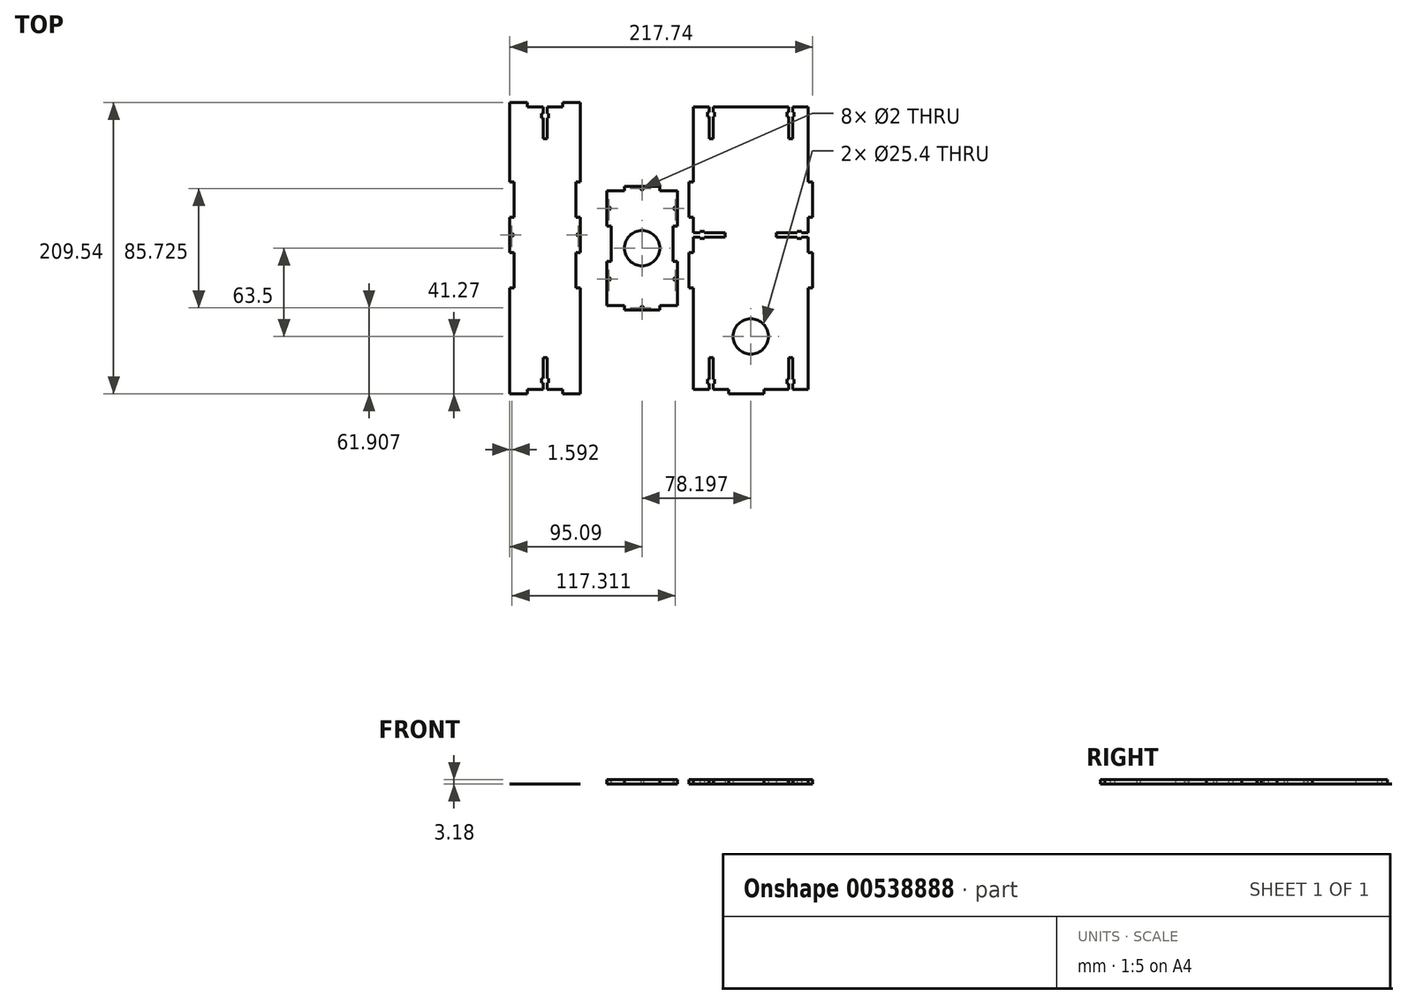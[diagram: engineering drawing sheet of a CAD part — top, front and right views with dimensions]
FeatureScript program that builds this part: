
annotation { "Feature Type Name" : "Feature", "Feature Type Description" : "" }
export const myFeature = defineFeature(function(context is Context, id is Id, definition is map)
    precondition{}
    {
        {
            var Q0;
            Q0=qCreatedBy(makeId("Top.planeOp"),FACE);
            var sketch = newSketch(context, id + "F0", { "sketchPlane" : qUnion([Q0])});
            skLineSegment(sketch, "E0.bottom", {"start": v(-22.22, 41.28) * mm, "end": v(-12.7, 41.28) * mm});
            skLineSegment(sketch, "E0.top", {"start": v(-22.23, -41.28) * mm, "end": v(-12.7, -41.28) * mm});
            skLineSegment(sketch, "E0.left", {"start": v(-22.22, 15.88) * mm, "end": v(-22.23, -9.52) * mm});
            skLineSegment(sketch, "E0.right", {"start": v(22.23, 15.88) * mm, "end": v(22.22, -9.52) * mm});
            skPoint(sketch, "E0.middle", {"position": v(0, 0) * mm});
            skLineSegment(sketch, "E1.bottom", {"start": v(-12.7, 44.45) * mm, "end": v(12.7, 44.45) * mm});
            skLineSegment(sketch, "E1.left", {"start": v(-12.7, 44.45) * mm, "end": v(-12.7, 41.28) * mm});
            skLineSegment(sketch, "E1.right", {"start": v(12.7, 44.45) * mm, "end": v(12.7, 41.28) * mm});
            skPoint(sketch, "E1.middle", {"position": v(0, 41.28) * mm});
            skPoint(sketch, "E2.orphan", {"position": v(12.7, 38.1) * mm});
            skPoint(sketch, "E3.orphan", {"position": v(-12.7, 38.1) * mm});
            skLineSegment(sketch, "E4.top", {"start": v(-12.7, -44.45) * mm, "end": v(12.7, -44.45) * mm});
            skLineSegment(sketch, "E4.left", {"start": v(-12.7, -41.28) * mm, "end": v(-12.7, -44.45) * mm});
            skLineSegment(sketch, "E4.right", {"start": v(12.7, -41.28) * mm, "end": v(12.7, -44.45) * mm});
            skPoint(sketch, "E4.middle", {"position": v(0, -41.27) * mm});
            skPoint(sketch, "E4.bottom.start.orphan", {"position": v(-12.7, -38.1) * mm});
            skPoint(sketch, "E5.orphan", {"position": v(12.7, -38.1) * mm});
            skLineSegment(sketch, "E6.bottom", {"start": v(-22.22, 41.28) * mm, "end": v(-25.4, 41.28) * mm});
            skLineSegment(sketch, "E6.top", {"start": v(-22.22, 15.88) * mm, "end": v(-25.4, 15.88) * mm});
            skLineSegment(sketch, "E6.right", {"start": v(-25.4, 41.28) * mm, "end": v(-25.4, 15.88) * mm});
            skPoint(sketch, "E7", {"position": v(-22.23, -9.52) * mm});
            skLineSegment(sketch, "E8.bottom", {"start": v(-22.23, -9.52) * mm, "end": v(-25.4, -9.52) * mm});
            skLineSegment(sketch, "E8.right", {"start": v(-25.4, -9.52) * mm, "end": v(-25.4, -34.92) * mm});
            skLineSegment(sketch, "E9.MirrorCS", {"start": v(25.4, 41.27) * mm, "end": v(25.4, 15.87) * mm});
            skLineSegment(sketch, "E10.MirrorCS", {"start": v(22.23, 41.28) * mm, "end": v(25.4, 41.28) * mm});
            skLineSegment(sketch, "E11.MirrorCS", {"start": v(22.23, 15.88) * mm, "end": v(25.4, 15.88) * mm});
            skLineSegment(sketch, "E12.MirrorCS", {"start": v(22.23, -9.52) * mm, "end": v(25.4, -9.52) * mm});
            skLineSegment(sketch, "E13.MirrorCS", {"start": v(25.4, -9.53) * mm, "end": v(25.4, -34.93) * mm});
            skLineSegment(sketch, "E14.trimOffspring", {"start": v(12.7, 41.28) * mm, "end": v(22.23, 41.28) * mm});
            skLineSegment(sketch, "E15.trimOffspring", {"start": v(12.7, -41.28) * mm, "end": v(22.23, -41.28) * mm});
            skLineSegment(sketch, "E16.top", {"start": v(-22.22, -41.28) * mm, "end": v(-25.4, -41.28) * mm});
            skLineSegment(sketch, "E16.right", {"start": v(-25.4, -34.92) * mm, "end": v(-25.4, -41.28) * mm});
            skLineSegment(sketch, "E17.bottom", {"start": v(22.22, -41.28) * mm, "end": v(25.4, -41.28) * mm});
            skLineSegment(sketch, "E17.right", {"start": v(25.4, -41.28) * mm, "end": v(25.4, -34.93) * mm});
            skCircle(sketch, "E18", {"center": v(0, 42.86) * mm, "radius": 1 * mm});
            skPoint(sketch, "E18.centerSnap0", {"position": v(-12.7, 42.86) * mm});
            skCircle(sketch, "E19", {"center": v(-23.81, 28.58) * mm, "radius": 1 * mm});
            skPoint(sketch, "E19.centerSnap0", {"position": v(-23.81, 41.28) * mm});
            skPoint(sketch, "E19.centerSnap1", {"position": v(-25.4, 28.58) * mm});
            skCircle(sketch, "E20", {"center": v(23.81, 28.57) * mm, "radius": 1 * mm});
            skPoint(sketch, "E20.centerSnap0", {"position": v(25.4, 28.57) * mm});
            skPoint(sketch, "E20.centerSnap1", {"position": v(23.81, 41.28) * mm});
            skCircle(sketch, "E21", {"center": v(0, -42.86) * mm, "radius": 1 * mm});
            skPoint(sketch, "E21.centerSnap0", {"position": v(0, -44.45) * mm});
            skPoint(sketch, "E21.centerSnap1", {"position": v(-12.7, -42.86) * mm});
            skCircle(sketch, "E22", {"center": v(-23.81, -22.22) * mm, "radius": 1 * mm});
            skPoint(sketch, "E22.centerSnap0", {"position": v(-23.81, -9.52) * mm});
            skPoint(sketch, "E22.centerSnap1", {"position": v(-25.4, -22.22) * mm});
            skCircle(sketch, "E23", {"center": v(23.81, -22.23) * mm, "radius": 1 * mm});
            skPoint(sketch, "E23.centerSnap0", {"position": v(23.81, -9.52) * mm});
            skPoint(sketch, "E23.centerSnap1", {"position": v(25.4, -22.23) * mm});
            skLineSegment(sketch, "E24.direction1", {"start": v(-25.4, -41.28) * mm, "end": v(228.6, -41.28) * mm, "construction": true});
            skCircle(sketch, "E25", {"center": v(0, 0) * mm, "radius": 12.7 * mm});
            skSolve(sketch);
        }
        {
            var Q0;
            Q0=qCreatedBy(makeId("Top.planeOp"),FACE);
            var sketch = newSketch(context, id + "F1", { "sketchPlane" : qUnion([Q0])});
            skLineSegment(sketch, "E26.bottom", {"start": v(-82.39, 101.6) * mm, "end": v(-56.99, 101.6) * mm});
            skLineSegment(sketch, "E26.top", {"start": v(-82.39, -101.6) * mm, "end": v(-56.99, -101.6) * mm});
            skLineSegment(sketch, "E26.left", {"start": v(-95.09, 101.6) * mm, "end": v(-95.09, 47.62) * mm});
            skLineSegment(sketch, "E26.right", {"start": v(-44.29, 101.6) * mm, "end": v(-44.29, 47.63) * mm});
            skPoint(sketch, "E26.middle", {"position": v(-69.69, 0) * mm});
            skLineSegment(sketch, "E27.bottom", {"start": v(-95.09, 104.78) * mm, "end": v(-82.39, 104.78) * mm});
            skLineSegment(sketch, "E27.left", {"start": v(-95.09, 104.78) * mm, "end": v(-95.09, 101.6) * mm});
            skLineSegment(sketch, "E27.right", {"start": v(-44.29, 104.78) * mm, "end": v(-44.29, 101.6) * mm});
            skPoint(sketch, "E27.middle", {"position": v(-69.69, 101.6) * mm});
            skPoint(sketch, "E27.top.start.orphan", {"position": v(-95.09, 98.43) * mm});
            skPoint(sketch, "E28.orphan", {"position": v(-44.29, 98.43) * mm});
            skPoint(sketch, "E29", {"position": v(-82.39, 104.78) * mm});
            skPoint(sketch, "E30", {"position": v(-56.99, 104.78) * mm});
            skLineSegment(sketch, "E31", {"start": v(-82.39, 104.78) * mm, "end": v(-82.39, 101.6) * mm});
            skLineSegment(sketch, "E32", {"start": v(-56.99, 104.78) * mm, "end": v(-56.99, 101.6) * mm});
            skLineSegment(sketch, "E33.trimOffspring", {"start": v(-56.99, 104.78) * mm, "end": v(-44.29, 104.78) * mm});
            skLineSegment(sketch, "E34.MirrorCS", {"start": v(-95.09, -104.78) * mm, "end": v(-82.39, -104.78) * mm});
            skLineSegment(sketch, "E35.MirrorCS", {"start": v(-95.09, -104.78) * mm, "end": v(-95.09, -101.6) * mm});
            skLineSegment(sketch, "E36.MirrorCS", {"start": v(-82.39, -104.78) * mm, "end": v(-82.39, -101.6) * mm});
            skLineSegment(sketch, "E37.MirrorCS", {"start": v(-56.99, -104.78) * mm, "end": v(-56.99, -101.6) * mm});
            skLineSegment(sketch, "E38.MirrorCS", {"start": v(-56.99, -104.78) * mm, "end": v(-44.29, -104.78) * mm});
            skLineSegment(sketch, "E39", {"start": v(-44.29, -104.78) * mm, "end": v(-44.29, -101.6) * mm});
            skPoint(sketch, "E40", {"position": v(-95.09, 47.63) * mm});
            skPoint(sketch, "E41", {"position": v(-95.09, -50.8) * mm});
            skLineSegment(sketch, "E42.bottom", {"start": v(-95.09, 47.63) * mm, "end": v(-91.91, 47.63) * mm});
            skLineSegment(sketch, "E42.top", {"start": v(-95.09, 22.23) * mm, "end": v(-91.91, 22.23) * mm});
            skLineSegment(sketch, "E42.right", {"start": v(-91.91, 47.63) * mm, "end": v(-91.91, 22.23) * mm});
            skLineSegment(sketch, "E43.bottom", {"start": v(-95.09, -3.17) * mm, "end": v(-91.91, -3.17) * mm});
            skLineSegment(sketch, "E43.top", {"start": v(-95.09, -28.58) * mm, "end": v(-91.91, -28.58) * mm});
            skLineSegment(sketch, "E43.right", {"start": v(-91.91, -3.17) * mm, "end": v(-91.91, -28.58) * mm});
            skLineSegment(sketch, "E44.trimOffspring", {"start": v(-95.09, -28.57) * mm, "end": v(-95.09, -101.6) * mm});
            skLineSegment(sketch, "E45.trimOffspring", {"start": v(-95.09, 22.23) * mm, "end": v(-95.09, -3.17) * mm});
            skLineSegment(sketch, "E46.MirrorCS", {"start": v(-47.46, 47.63) * mm, "end": v(-47.46, 22.23) * mm});
            skLineSegment(sketch, "E47.MirrorCS", {"start": v(-47.46, -3.17) * mm, "end": v(-47.46, -28.57) * mm});
            skLineSegment(sketch, "E48.MirrorCS", {"start": v(-44.29, 47.63) * mm, "end": v(-47.46, 47.63) * mm});
            skLineSegment(sketch, "E49.MirrorCS", {"start": v(-44.29, 22.23) * mm, "end": v(-47.46, 22.23) * mm});
            skLineSegment(sketch, "E50.trimOffspring", {"start": v(-44.29, 22.23) * mm, "end": v(-44.29, -3.17) * mm});
            skPoint(sketch, "E51", {"position": v(-44.29, -3.17) * mm});
            skPoint(sketch, "E52", {"position": v(-44.29, -28.57) * mm});
            skLineSegment(sketch, "E53.trimOffspring", {"start": v(-44.29, -28.57) * mm, "end": v(-44.29, -101.6) * mm});
            skLineSegment(sketch, "E54", {"start": v(-44.29, -3.17) * mm, "end": v(-47.46, -3.17) * mm});
            skLineSegment(sketch, "E55", {"start": v(-47.46, -28.57) * mm, "end": v(-44.29, -28.57) * mm});
            skPoint(sketch, "E56.orphan", {"position": v(-44.29, 0) * mm});
            skPoint(sketch, "E57.start.orphan", {"position": v(-95.09, 0) * mm});
            skLineSegment(sketch, "E58.bottom", {"start": v(-71.19, 78.7) * mm, "end": v(-68.19, 78.74) * mm});
            skLineSegment(sketch, "E58.left", {"start": v(-71.19, 78.7) * mm, "end": v(-71.19, 93.66) * mm});
            skLineSegment(sketch, "E58.right", {"start": v(-68.19, 78.74) * mm, "end": v(-68.19, 93.66) * mm});
            skPoint(sketch, "E58.top.end.orphan", {"position": v(-68.19, 124.5) * mm});
            skPoint(sketch, "E59.orphan", {"position": v(-71.19, 124.46) * mm});
            skLineSegment(sketch, "E60.bottom", {"start": v(-72.23, 96.84) * mm, "end": v(-71.19, 96.84) * mm});
            skLineSegment(sketch, "E60.top", {"start": v(-72.23, 93.66) * mm, "end": v(-71.19, 93.66) * mm});
            skLineSegment(sketch, "E60.left", {"start": v(-72.23, 96.84) * mm, "end": v(-72.23, 93.66) * mm});
            skLineSegment(sketch, "E60.right", {"start": v(-67.15, 96.84) * mm, "end": v(-67.15, 93.66) * mm});
            skPoint(sketch, "E60.middle", {"position": v(-69.69, 95.25) * mm});
            skLineSegment(sketch, "E61.trimOffspring", {"start": v(-68.19, 96.84) * mm, "end": v(-67.15, 96.84) * mm});
            skLineSegment(sketch, "E62.trimOffspring", {"start": v(-68.19, 93.66) * mm, "end": v(-67.15, 93.66) * mm});
            skLineSegment(sketch, "E63.trimOffspring", {"start": v(-71.19, 96.84) * mm, "end": v(-71.19, 101.6) * mm});
            skLineSegment(sketch, "E64.trimOffspring", {"start": v(-68.19, 96.84) * mm, "end": v(-68.19, 101.6) * mm});
            skLineSegment(sketch, "E65.MirrorCS", {"start": v(-71.19, -78.7) * mm, "end": v(-71.19, -93.66) * mm});
            skLineSegment(sketch, "E66.MirrorCS", {"start": v(-68.19, -78.74) * mm, "end": v(-68.19, -93.66) * mm});
            skLineSegment(sketch, "E67.MirrorCS", {"start": v(-71.19, -78.7) * mm, "end": v(-68.19, -78.74) * mm});
            skLineSegment(sketch, "E68.MirrorCS", {"start": v(-67.15, -96.84) * mm, "end": v(-67.15, -93.66) * mm});
            skLineSegment(sketch, "E69.MirrorCS", {"start": v(-72.23, -96.84) * mm, "end": v(-72.23, -93.66) * mm});
            skLineSegment(sketch, "E70.MirrorCS", {"start": v(-71.19, -96.84) * mm, "end": v(-71.19, -101.6) * mm});
            skLineSegment(sketch, "E71.MirrorCS", {"start": v(-68.19, -96.84) * mm, "end": v(-68.19, -101.6) * mm});
            skLineSegment(sketch, "E72.MirrorCS", {"start": v(-72.23, -96.84) * mm, "end": v(-71.19, -96.84) * mm});
            skLineSegment(sketch, "E73.MirrorCS", {"start": v(-72.23, -93.66) * mm, "end": v(-71.19, -93.66) * mm});
            skLineSegment(sketch, "E74.MirrorCS", {"start": v(-68.19, -93.66) * mm, "end": v(-67.15, -93.66) * mm});
            skLineSegment(sketch, "E75.MirrorCS", {"start": v(-68.19, -96.84) * mm, "end": v(-67.15, -96.84) * mm});
            skCircle(sketch, "E76", {"center": v(-93.5, 9.53) * mm, "radius": 1 * mm});
            skPoint(sketch, "E76.centerSnap0", {"position": v(-93.5, 22.23) * mm});
            skPoint(sketch, "E76.centerSnap1", {"position": v(-95.09, 9.53) * mm});
            skCircle(sketch, "E77", {"center": v(-45.87, 9.53) * mm, "radius": 1 * mm});
            skPoint(sketch, "E77.centerSnap0", {"position": v(-45.87, 22.23) * mm});
            skPoint(sketch, "E77.centerSnap1", {"position": v(-44.29, 9.53) * mm});
            skSolve(sketch);
        }
        {
            var Q0;
            Q0 = qSketchRegion(id + "F0", true);
            extrude(context, id + "F2", {"entities" : qUnion([Q0]), "depth" : 3.17 * mm, "offsetDistance" : 25.4 * mm});
        }
        {
            var Q0;
            Q0=makeQuery(id+"F1.imprint","IMPRINT",FACE,{"disambiguationData":[TD([[makeQuery(id+"F1.imprint","IMPRINT",EDGE,{"derivedFrom":sQuery(id+"F1.wireOp",EDGE,"E26.bottom")}),-1.0]])]});
            extrude(context, id + "F3", {"entities" : qUnion([Q0]), "depth" : 1 / 203.2 * mm, "offsetDistance" : 25.4 * mm});
        }
        {
            var Q0;
            Q0=qCreatedBy(makeId("Top.planeOp"),FACE);
            var sketch = newSketch(context, id + "F4", { "sketchPlane" : qUnion([Q0])});
            skLineSegment(sketch, "E78.bottom", {"start": v(36.92, 101.6) * mm, "end": v(119.47, 101.6) * mm});
            skLineSegment(sketch, "E78.top", {"start": v(36.92, -101.6) * mm, "end": v(119.47, -101.6) * mm});
            skLineSegment(sketch, "E78.left", {"start": v(36.92, 101.6) * mm, "end": v(36.92, 47.63) * mm});
            skLineSegment(sketch, "E78.right", {"start": v(119.47, 101.6) * mm, "end": v(119.47, 47.63) * mm});
            skPoint(sketch, "E78.middle", {"position": v(78.2, 0) * mm});
            skPoint(sketch, "E79", {"position": v(62.32, 101.6) * mm});
            skLineSegment(sketch, "E80.bottom", {"start": v(62.32, 101.6) * mm, "end": v(87.72, 101.6) * mm});
            skLineSegment(sketch, "E80.top", {"start": v(62.32, 104.78) * mm, "end": v(87.72, 104.78) * mm});
            skLineSegment(sketch, "E80.left", {"start": v(62.32, 101.6) * mm, "end": v(62.32, 104.78) * mm});
            skLineSegment(sketch, "E80.right", {"start": v(87.72, 101.6) * mm, "end": v(87.72, 104.78) * mm});
            skLineSegment(sketch, "E81.MirrorCS", {"start": v(62.32, -104.78) * mm, "end": v(87.72, -104.78) * mm});
            skLineSegment(sketch, "E82.MirrorCS", {"start": v(62.32, -101.6) * mm, "end": v(62.32, -104.78) * mm});
            skLineSegment(sketch, "E83.MirrorCS", {"start": v(87.72, -101.6) * mm, "end": v(87.72, -104.78) * mm});
            skPoint(sketch, "E84", {"position": v(36.92, 98.43) * mm});
            skLineSegment(sketch, "E85.bottom", {"start": v(36.92, 47.62) * mm, "end": v(33.75, 47.62) * mm});
            skLineSegment(sketch, "E85.top", {"start": v(36.92, 22.22) * mm, "end": v(33.75, 22.22) * mm});
            skLineSegment(sketch, "E85.right", {"start": v(33.75, 47.63) * mm, "end": v(33.75, 22.23) * mm});
            skLineSegment(sketch, "E86.trimOffspring", {"start": v(36.92, 22.22) * mm, "end": v(36.92, -3.18) * mm});
            skLineSegment(sketch, "E87.bottom", {"start": v(36.92, -3.17) * mm, "end": v(33.75, -3.17) * mm});
            skLineSegment(sketch, "E87.top", {"start": v(36.92, -28.58) * mm, "end": v(33.75, -28.58) * mm});
            skLineSegment(sketch, "E87.right", {"start": v(33.75, -3.18) * mm, "end": v(33.75, -28.58) * mm});
            skLineSegment(sketch, "E88.MirrorCS", {"start": v(122.65, 47.63) * mm, "end": v(122.65, 22.23) * mm});
            skLineSegment(sketch, "E89.MirrorCS", {"start": v(122.65, -3.18) * mm, "end": v(122.65, -28.58) * mm});
            skLineSegment(sketch, "E90.MirrorCS", {"start": v(119.47, -3.17) * mm, "end": v(122.65, -3.17) * mm});
            skLineSegment(sketch, "E91.MirrorCS", {"start": v(119.47, 22.23) * mm, "end": v(122.65, 22.23) * mm});
            skLineSegment(sketch, "E92.MirrorCS", {"start": v(119.47, 47.63) * mm, "end": v(122.65, 47.63) * mm});
            skLineSegment(sketch, "E93.MirrorCS", {"start": v(119.47, -28.57) * mm, "end": v(122.65, -28.57) * mm});
            skLineSegment(sketch, "E94.trimOffspring", {"start": v(36.92, -28.58) * mm, "end": v(36.92, -101.6) * mm});
            skLineSegment(sketch, "E95.trimOffspring", {"start": v(119.47, -28.58) * mm, "end": v(119.47, -101.6) * mm});
            skLineSegment(sketch, "E96.trimOffspring", {"start": v(119.47, 22.22) * mm, "end": v(119.47, -3.17) * mm});
            skLineSegment(sketch, "E97.bottom", {"start": v(36.92, 11.02) * mm, "end": v(41.68, 11.02) * mm});
            skLineSegment(sketch, "E97.top", {"start": v(36.92, 8.03) * mm, "end": v(41.68, 8.03) * mm});
            skLineSegment(sketch, "E97.right", {"start": v(59.78, 11.02) * mm, "end": v(59.8, 8.03) * mm});
            skPoint(sketch, "E97.middle", {"position": v(36.92, 9.53) * mm});
            skPoint(sketch, "E97.left.start.orphan", {"position": v(14.04, 11.02) * mm});
            skPoint(sketch, "E98.orphan", {"position": v(14.06, 8.03) * mm});
            skLineSegment(sketch, "E99.bottom", {"start": v(41.68, 12.07) * mm, "end": v(44.86, 12.07) * mm});
            skLineSegment(sketch, "E99.top", {"start": v(41.68, 6.99) * mm, "end": v(44.86, 6.99) * mm});
            skLineSegment(sketch, "E99.left", {"start": v(41.68, 12.07) * mm, "end": v(41.68, 11.02) * mm});
            skLineSegment(sketch, "E99.right", {"start": v(44.86, 12.07) * mm, "end": v(44.86, 11.02) * mm});
            skPoint(sketch, "E99.middle", {"position": v(43.27, 9.53) * mm});
            skLineSegment(sketch, "E100.trimOffspring", {"start": v(41.68, 8.03) * mm, "end": v(41.68, 6.99) * mm});
            skLineSegment(sketch, "E101.trimOffspring", {"start": v(44.86, 8.03) * mm, "end": v(44.86, 6.99) * mm});
            skLineSegment(sketch, "E102.trimOffspring", {"start": v(44.86, 11.02) * mm, "end": v(59.78, 11.02) * mm});
            skLineSegment(sketch, "E103.trimOffspring", {"start": v(44.86, 8.03) * mm, "end": v(59.8, 8.03) * mm});
            skPoint(sketch, "E104.orphan", {"position": v(96.61, 11.02) * mm});
            skPoint(sketch, "E105.MirrorCS.end.orphan", {"position": v(111.53, 12.07) * mm});
            skPoint(sketch, "E105.MirrorCS.start.orphan", {"position": v(114.7, 12.07) * mm});
            skPoint(sketch, "E106.MirrorCS.start.orphan", {"position": v(119.47, 11.02) * mm});
            skPoint(sketch, "E107.MirrorCS.end.orphan", {"position": v(114.7, 6.99) * mm});
            skLineSegment(sketch, "E108.MirrorCS", {"start": v(111.53, 11.02) * mm, "end": v(96.61, 11.02) * mm});
            skLineSegment(sketch, "E109.MirrorCS", {"start": v(111.53, 8.03) * mm, "end": v(96.59, 8.03) * mm});
            skLineSegment(sketch, "E110.MirrorCS", {"start": v(96.61, 11.02) * mm, "end": v(96.59, 8.03) * mm});
            skLineSegment(sketch, "E111.MirrorCS", {"start": v(114.7, 12.07) * mm, "end": v(111.53, 12.07) * mm});
            skLineSegment(sketch, "E112.MirrorCS", {"start": v(114.7, 6.99) * mm, "end": v(111.53, 6.99) * mm});
            skLineSegment(sketch, "E113.MirrorCS", {"start": v(111.53, 8.03) * mm, "end": v(111.53, 6.99) * mm});
            skLineSegment(sketch, "E114.MirrorCS", {"start": v(111.53, 12.07) * mm, "end": v(111.53, 11.02) * mm});
            skLineSegment(sketch, "E115.MirrorCS", {"start": v(114.7, 12.07) * mm, "end": v(114.7, 11.02) * mm});
            skLineSegment(sketch, "E116.MirrorCS", {"start": v(114.7, 8.03) * mm, "end": v(114.7, 6.99) * mm});
            skLineSegment(sketch, "E117.MirrorCS", {"start": v(119.47, 8.03) * mm, "end": v(114.7, 8.03) * mm});
            skLineSegment(sketch, "E118.MirrorCS", {"start": v(119.47, 11.02) * mm, "end": v(114.7, 11.02) * mm});
            skPoint(sketch, "E119.orphan", {"position": v(78.2, -101.6) * mm});
            skPoint(sketch, "E120.start.orphan", {"position": v(78.2, 101.6) * mm});
            skPoint(sketch, "E121", {"position": v(49.62, 101.6) * mm});
            skLineSegment(sketch, "E122.top", {"start": v(48.12, 78.74) * mm, "end": v(51.12, 78.74) * mm});
            skLineSegment(sketch, "E122.left", {"start": v(48.12, 101.6) * mm, "end": v(48.12, 97.62) * mm});
            skLineSegment(sketch, "E122.right", {"start": v(51.12, 101.6) * mm, "end": v(51.12, 97.62) * mm});
            skPoint(sketch, "E123.orphan", {"position": v(51.12, 124.46) * mm});
            skPoint(sketch, "E124.orphan", {"position": v(48.12, 124.46) * mm});
            skLineSegment(sketch, "E125.bottom", {"start": v(47.08, 97.62) * mm, "end": v(48.12, 97.62) * mm});
            skLineSegment(sketch, "E125.left", {"start": v(47.08, 97.62) * mm, "end": v(47.08, 94.44) * mm});
            skLineSegment(sketch, "E125.right", {"start": v(52.16, 97.62) * mm, "end": v(52.16, 94.44) * mm});
            skPoint(sketch, "E125.middle", {"position": v(49.62, 96.03) * mm});
            skLineSegment(sketch, "E126.trimOffspring", {"start": v(51.12, 97.62) * mm, "end": v(52.16, 97.62) * mm});
            skLineSegment(sketch, "E127.trimOffspring", {"start": v(51.12, 94.44) * mm, "end": v(52.16, 94.44) * mm});
            skLineSegment(sketch, "E128", {"start": v(47.08, 94.44) * mm, "end": v(48.12, 94.44) * mm});
            skLineSegment(sketch, "E129.trimOffspring", {"start": v(48.12, 94.44) * mm, "end": v(48.12, 78.74) * mm});
            skLineSegment(sketch, "E130.trimOffspring", {"start": v(51.12, 94.44) * mm, "end": v(51.12, 78.74) * mm});
            skLineSegment(sketch, "E131.MirrorCS", {"start": v(105.27, 94.44) * mm, "end": v(105.27, 78.74) * mm});
            skLineSegment(sketch, "E132.MirrorCS", {"start": v(108.27, 94.44) * mm, "end": v(108.27, 78.74) * mm});
            skLineSegment(sketch, "E133.MirrorCS", {"start": v(108.27, 78.74) * mm, "end": v(105.27, 78.74) * mm});
            skLineSegment(sketch, "E134.MirrorCS", {"start": v(108.27, 101.6) * mm, "end": v(108.27, 97.62) * mm});
            skLineSegment(sketch, "E135.MirrorCS", {"start": v(105.27, 101.6) * mm, "end": v(105.27, 97.62) * mm});
            skLineSegment(sketch, "E136.MirrorCS", {"start": v(109.31, 97.62) * mm, "end": v(109.31, 94.44) * mm});
            skLineSegment(sketch, "E137.MirrorCS", {"start": v(104.23, 97.62) * mm, "end": v(104.23, 94.44) * mm});
            skLineSegment(sketch, "E138.MirrorCS", {"start": v(109.31, 97.62) * mm, "end": v(108.27, 97.62) * mm});
            skLineSegment(sketch, "E139.MirrorCS", {"start": v(105.27, 97.62) * mm, "end": v(104.23, 97.62) * mm});
            skLineSegment(sketch, "E140.MirrorCS", {"start": v(105.27, 94.44) * mm, "end": v(104.23, 94.44) * mm});
            skLineSegment(sketch, "E141.MirrorCS", {"start": v(109.31, 94.44) * mm, "end": v(108.27, 94.44) * mm});
            skLineSegment(sketch, "E142.MirrorCS", {"start": v(105.27, -94.44) * mm, "end": v(105.27, -78.74) * mm});
            skLineSegment(sketch, "E143.MirrorCS", {"start": v(108.27, -94.44) * mm, "end": v(108.27, -78.74) * mm});
            skLineSegment(sketch, "E144.MirrorCS", {"start": v(108.27, -78.74) * mm, "end": v(105.27, -78.74) * mm});
            skLineSegment(sketch, "E145.MirrorCS", {"start": v(104.23, -97.62) * mm, "end": v(104.23, -94.44) * mm});
            skLineSegment(sketch, "E146.MirrorCS", {"start": v(109.31, -97.62) * mm, "end": v(109.31, -94.44) * mm});
            skLineSegment(sketch, "E147.MirrorCS", {"start": v(105.27, -101.6) * mm, "end": v(105.27, -97.62) * mm});
            skLineSegment(sketch, "E148.MirrorCS", {"start": v(108.27, -101.6) * mm, "end": v(108.27, -97.62) * mm});
            skLineSegment(sketch, "E149.MirrorCS", {"start": v(105.27, -97.62) * mm, "end": v(104.23, -97.62) * mm});
            skLineSegment(sketch, "E150.MirrorCS", {"start": v(109.31, -97.62) * mm, "end": v(108.27, -97.62) * mm});
            skLineSegment(sketch, "E151.MirrorCS", {"start": v(109.31, -94.44) * mm, "end": v(108.27, -94.44) * mm});
            skLineSegment(sketch, "E152.MirrorCS", {"start": v(105.27, -94.44) * mm, "end": v(104.23, -94.44) * mm});
            skLineSegment(sketch, "E153.MirrorCS", {"start": v(47.08, -97.62) * mm, "end": v(47.08, -94.44) * mm});
            skLineSegment(sketch, "E154.MirrorCS", {"start": v(47.08, -94.44) * mm, "end": v(48.12, -94.44) * mm});
            skLineSegment(sketch, "E155.MirrorCS", {"start": v(47.08, -97.62) * mm, "end": v(48.12, -97.62) * mm});
            skLineSegment(sketch, "E156.MirrorCS", {"start": v(48.12, -94.44) * mm, "end": v(48.12, -78.74) * mm});
            skLineSegment(sketch, "E157.MirrorCS", {"start": v(48.12, -78.74) * mm, "end": v(51.12, -78.74) * mm});
            skLineSegment(sketch, "E158.MirrorCS", {"start": v(51.12, -94.44) * mm, "end": v(51.12, -78.74) * mm});
            skLineSegment(sketch, "E159.MirrorCS", {"start": v(51.12, -94.44) * mm, "end": v(52.16, -94.44) * mm});
            skLineSegment(sketch, "E160.MirrorCS", {"start": v(52.16, -97.62) * mm, "end": v(52.16, -94.44) * mm});
            skLineSegment(sketch, "E161.MirrorCS", {"start": v(51.12, -97.62) * mm, "end": v(52.16, -97.62) * mm});
            skLineSegment(sketch, "E162.MirrorCS", {"start": v(51.12, -101.6) * mm, "end": v(51.12, -97.62) * mm});
            skLineSegment(sketch, "E163.MirrorCS", {"start": v(48.12, -101.6) * mm, "end": v(48.12, -97.62) * mm});
            skPoint(sketch, "E164.orphan", {"position": v(36.92, 0) * mm});
            skPoint(sketch, "E165.end.orphan", {"position": v(119.47, 0) * mm});
            skCircle(sketch, "E166", {"center": v(78.2, -63.5) * mm, "radius": 12.7 * mm});
            skSolve(sketch);
        }
        {
            var Q0;
            {var subQ16=sQuery(id+"F4.wireOp",EDGE,"E78.left");Q0=makeQuery(id+"F4.imprint","IMPRINT",FACE,{"disambiguationData":[TD([[makeQuery(id+"F4.imprint","IMPRINT",EDGE,{"derivedFrom":subQ16}),1.0]])]});}
            var Q1;
            Q1=makeQuery(id+"F4.imprint","IMPRINT",FACE,{"disambiguationData":[TD([[makeQuery(id+"F4.imprint","IMPRINT",EDGE,{"derivedFrom":sQuery(id+"F4.wireOp",EDGE,"E81.MirrorCS")}),1.0]])]});
            var Q2;
            Q2=makeQuery(id+"F4.imprint","IMPRINT",FACE,{"disambiguationData":[TD([[makeQuery(id+"F4.imprint","IMPRINT",EDGE,{"derivedFrom":sQuery(id+"F4.wireOp",EDGE,"E80.bottom")}),1.0]])]});
            extrude(context, id + "F5", {"entities" : qUnion([Q0, Q1, Q2]), "depth" : 3.17 * mm, "offsetDistance" : 25.4 * mm});
        }
    });
